# Revit family: Clevis Hanger Support with Spring
name_source: partatom
category: Pipe Fittings
revit_build: Autodesk Revit 2014 (Build: 20130308_1515(x64)
units: mm (PartAtom-declared; Revit-internal decimal feet)

## types (22) — shared parameters
Fasteners = Fasteners
Neoprene Pad = Rubber
Pipe Support = Pipe Support
Spring = Spring

## per-type parameters (varying)
| type | Anchor Bolt | Bolt Size | Dim_A | Dim_A2 | Dim_G | Dim_G2 | Dim_G3 | Dim_G4 | Dim_T1 | Dim_T2 | Dim_W1 | Pipe OD |
| 15 | Nut : M10 | Nut2 : M6 | 10 mm  [stored 0.0328084 ft] | 20 mm  [stored 0.0656168 ft] | 6 mm  [stored 0.019685 ft] | 6 mm  [stored 0.019685 ft] | 12 mm  [stored 0.0393701 ft] | 5 mm  [stored 0.0164042 ft] | 3 mm  [stored 0.00984252 ft] | 3 mm  [stored 0.00984252 ft] | 25 mm  [stored 0.082021 ft] | 21 mm |
| 20 | Nut : M10 | Nut2 : M6 | 10 mm  [stored 0.0328084 ft] | 20 mm  [stored 0.0656168 ft] | 6 mm  [stored 0.019685 ft] | 6 mm  [stored 0.019685 ft] | 12 mm  [stored 0.0393701 ft] | 5 mm  [stored 0.0164042 ft] | 3 mm  [stored 0.00984252 ft] | 3 mm  [stored 0.00984252 ft] | 25 mm  [stored 0.082021 ft] | 27 mm |
| 25 | Nut : M10 | Nut2 : M6 | 10 mm  [stored 0.0328084 ft] | 20 mm  [stored 0.0656168 ft] | 6 mm  [stored 0.019685 ft] | 6 mm  [stored 0.019685 ft] | 12 mm  [stored 0.0393701 ft] | 5 mm  [stored 0.0164042 ft] | 3 mm  [stored 0.00984252 ft] | 3 mm  [stored 0.00984252 ft] | 25 mm  [stored 0.082021 ft] | 33 mm |
| 32 | Nut : M10 | Nut2 : M6 | 10 mm  [stored 0.0328084 ft] | 20 mm  [stored 0.0656168 ft] | 6 mm  [stored 0.019685 ft] | 6 mm  [stored 0.019685 ft] | 12 mm  [stored 0.0393701 ft] | 5 mm  [stored 0.0164042 ft] | 3 mm  [stored 0.00984252 ft] | 3 mm  [stored 0.00984252 ft] | 25 mm  [stored 0.082021 ft] | 42 mm |
| 40 | Nut : M10 | Nut2 : M6 | 10 mm  [stored 0.0328084 ft] | 20 mm  [stored 0.0656168 ft] | 6 mm  [stored 0.019685 ft] | 6 mm  [stored 0.019685 ft] | 12 mm  [stored 0.0393701 ft] | 5 mm  [stored 0.0164042 ft] | 3 mm  [stored 0.00984252 ft] | 3 mm  [stored 0.00984252 ft] | 25 mm  [stored 0.082021 ft] | 48 mm |
| 50 | Nut : M10 | Nut2 : M6 | 10 mm  [stored 0.0328084 ft] | 20 mm  [stored 0.0656168 ft] | 6 mm  [stored 0.019685 ft] | 6 mm  [stored 0.019685 ft] | 12 mm  [stored 0.0393701 ft] | 5 mm  [stored 0.0164042 ft] | 3 mm  [stored 0.00984252 ft] | 3 mm  [stored 0.00984252 ft] | 25 mm  [stored 0.082021 ft] | 60 mm |
| 65 | Nut : M12 | Nut2 : M10 | 12 mm  [stored 0.0393701 ft] | 24 mm  [stored 0.0787402 ft] | 10 mm  [stored 0.0328084 ft] | 10 mm  [stored 0.0328084 ft] | 20 mm  [stored 0.0656168 ft] | 8 mm  [stored 0.0262467 ft] | 5 mm  [stored 0.0164042 ft] | 5 mm  [stored 0.0164042 ft] | 32 mm  [stored 0.104987 ft] | 73 mm  [stored 0.239501 ft] |
| 80 | Nut : M12 | Nut2 : M10 | 12 mm  [stored 0.0393701 ft] | 24 mm  [stored 0.0787402 ft] | 10 mm  [stored 0.0328084 ft] | 10 mm  [stored 0.0328084 ft] | 20 mm  [stored 0.0656168 ft] | 8 mm  [stored 0.0262467 ft] | 5 mm  [stored 0.0164042 ft] | 5 mm  [stored 0.0164042 ft] | 32 mm  [stored 0.104987 ft] | 89 mm |
| 90 | Nut : M12 | Nut2 : M10 | 12 mm  [stored 0.0393701 ft] | 24 mm  [stored 0.0787402 ft] | 10 mm  [stored 0.0328084 ft] | 10 mm  [stored 0.0328084 ft] | 20 mm  [stored 0.0656168 ft] | 8 mm  [stored 0.0262467 ft] | 5 mm  [stored 0.0164042 ft] | 5 mm  [stored 0.0164042 ft] | 32 mm  [stored 0.104987 ft] | 102 mm |
| 100 | Nut : M16 | Nut2 : M10 | 16 mm  [stored 0.0524934 ft] | 32 mm  [stored 0.104987 ft] | 10 mm  [stored 0.0328084 ft] | 10 mm  [stored 0.0328084 ft] | 20 mm  [stored 0.0656168 ft] | 8 mm  [stored 0.0262467 ft] | 6 mm  [stored 0.019685 ft] | 5 mm  [stored 0.0164042 ft] | 32 mm  [stored 0.104987 ft] | 114 mm |
| 125 | Nut : M12 | Nut2 : M12 | 16 mm  [stored 0.0524934 ft] | 32 mm  [stored 0.104987 ft] | 12 mm  [stored 0.0393701 ft] | 12 mm  [stored 0.0393701 ft] | 24 mm  [stored 0.0787402 ft] | 10 mm  [stored 0.0328084 ft] | 6 mm  [stored 0.019685 ft] | 5 mm  [stored 0.0164042 ft] | 32 mm  [stored 0.104987 ft] | 141 mm |
| 150 | Nut : M20 | Nut2 : M12 | 20 mm  [stored 0.0656168 ft] | 40 mm  [stored 0.131234 ft] | 12 mm  [stored 0.0393701 ft] | 12 mm  [stored 0.0393701 ft] | 24 mm  [stored 0.0787402 ft] | 10 mm  [stored 0.0328084 ft] | 6 mm  [stored 0.019685 ft] | 5 mm  [stored 0.0164042 ft] | 38 mm | 168 mm |
| 200 | Nut : M22 | Nut2 : M16 | 22 mm  [stored 0.0721785 ft] | 44 mm  [stored 0.144357 ft] | 16 mm  [stored 0.0524934 ft] | 16 mm  [stored 0.0524934 ft] | 32 mm  [stored 0.104987 ft] | 13 mm | 6 mm  [stored 0.019685 ft] | 5 mm  [stored 0.0164042 ft] | 45 mm  [stored 0.147638 ft] | 219 mm |
| 250 | Nut : M22 | Nut2 : M20 | 22 mm  [stored 0.0721785 ft] | 44 mm  [stored 0.144357 ft] | 20 mm  [stored 0.0656168 ft] | 20 mm  [stored 0.0656168 ft] | 40 mm  [stored 0.131234 ft] | 16 mm  [stored 0.0524934 ft] | 10 mm  [stored 0.0328084 ft] | 6 mm  [stored 0.019685 ft] | 45 mm  [stored 0.147638 ft] | 273 mm |
| 300 | Nut : M22 | Nut2 : M20 | 22 mm  [stored 0.0721785 ft] | 44 mm  [stored 0.144357 ft] | 20 mm  [stored 0.0656168 ft] | 20 mm  [stored 0.0656168 ft] | 40 mm  [stored 0.131234 ft] | 16 mm  [stored 0.0524934 ft] | 10 mm  [stored 0.0328084 ft] | 6 mm  [stored 0.019685 ft] | 51 mm | 324 mm |
| 350 | Nut : M25 | Nut2 : M22 | 25 mm  [stored 0.082021 ft] | 50 mm  [stored 0.164042 ft] | 22 mm  [stored 0.0721785 ft] | 22 mm  [stored 0.0721785 ft] | 44 mm  [stored 0.144357 ft] | 18 mm | 13 mm | 6 mm  [stored 0.019685 ft] | 51 mm | 356 mm |
| 400 | Nut : M25 | Nut2 : M25 | 25 mm  [stored 0.082021 ft] | 50 mm  [stored 0.164042 ft] | 25 mm  [stored 0.082021 ft] | 25 mm  [stored 0.082021 ft] | 50 mm  [stored 0.164042 ft] | 20 mm  [stored 0.0656168 ft] | 13 mm | 6 mm  [stored 0.019685 ft] | 64 mm  [stored 0.209974 ft] | 406 mm |
| 450 | Nut : M25 | Nut2 : M28 | 25 mm  [stored 0.082021 ft] | 50 mm  [stored 0.164042 ft] | 28 mm  [stored 0.0918635 ft] | 28 mm  [stored 0.0918635 ft] | 56 mm  [stored 0.183727 ft] | 22 mm  [stored 0.0721785 ft] | 13 mm | 6 mm  [stored 0.019685 ft] | 64 mm  [stored 0.209974 ft] | 457 mm |
| 500 | Nut : M32 | Nut2 : M32 | 32 mm  [stored 0.104987 ft] | 64 mm  [stored 0.209974 ft] | 32 mm  [stored 0.104987 ft] | 32 mm  [stored 0.104987 ft] | 64 mm  [stored 0.209974 ft] | 26 mm | 19 mm | 10 mm  [stored 0.0328084 ft] | 76 mm | 508 mm |
| 600 | Nut : M32 | Nut2 : M32 | 32 mm  [stored 0.104987 ft] | 64 mm  [stored 0.209974 ft] | 32 mm  [stored 0.104987 ft] | 32 mm  [stored 0.104987 ft] | 64 mm  [stored 0.209974 ft] | 26 mm | 19 mm | 10 mm  [stored 0.0328084 ft] | 76 mm | 610 mm |
| 750 | Nut : M32 | Nut2 : M32 | 32 mm  [stored 0.104987 ft] | 64 mm  [stored 0.209974 ft] | 32 mm  [stored 0.104987 ft] | 32 mm  [stored 0.104987 ft] | 64 mm  [stored 0.209974 ft] | 26 mm | 25 mm  [stored 0.082021 ft] | 10 mm  [stored 0.0328084 ft] | 76 mm | 813 mm |
| 900 | Nut : M32 | Nut2 : M32 | 32 mm  [stored 0.104987 ft] | 64 mm  [stored 0.209974 ft] | 32 mm  [stored 0.104987 ft] | 32 mm  [stored 0.104987 ft] | 64 mm  [stored 0.209974 ft] | 26 mm | 25 mm  [stored 0.082021 ft] | 10 mm  [stored 0.0328084 ft] | 76 mm | 973 mm |

note: [stored X ft] marks values corroborated as IEEE doubles in the binary element streams (Revit-internal decimal feet)

## geometry (parser evidence)
native form markers: Sweep x6
no freeform markers — native parametric forms only
